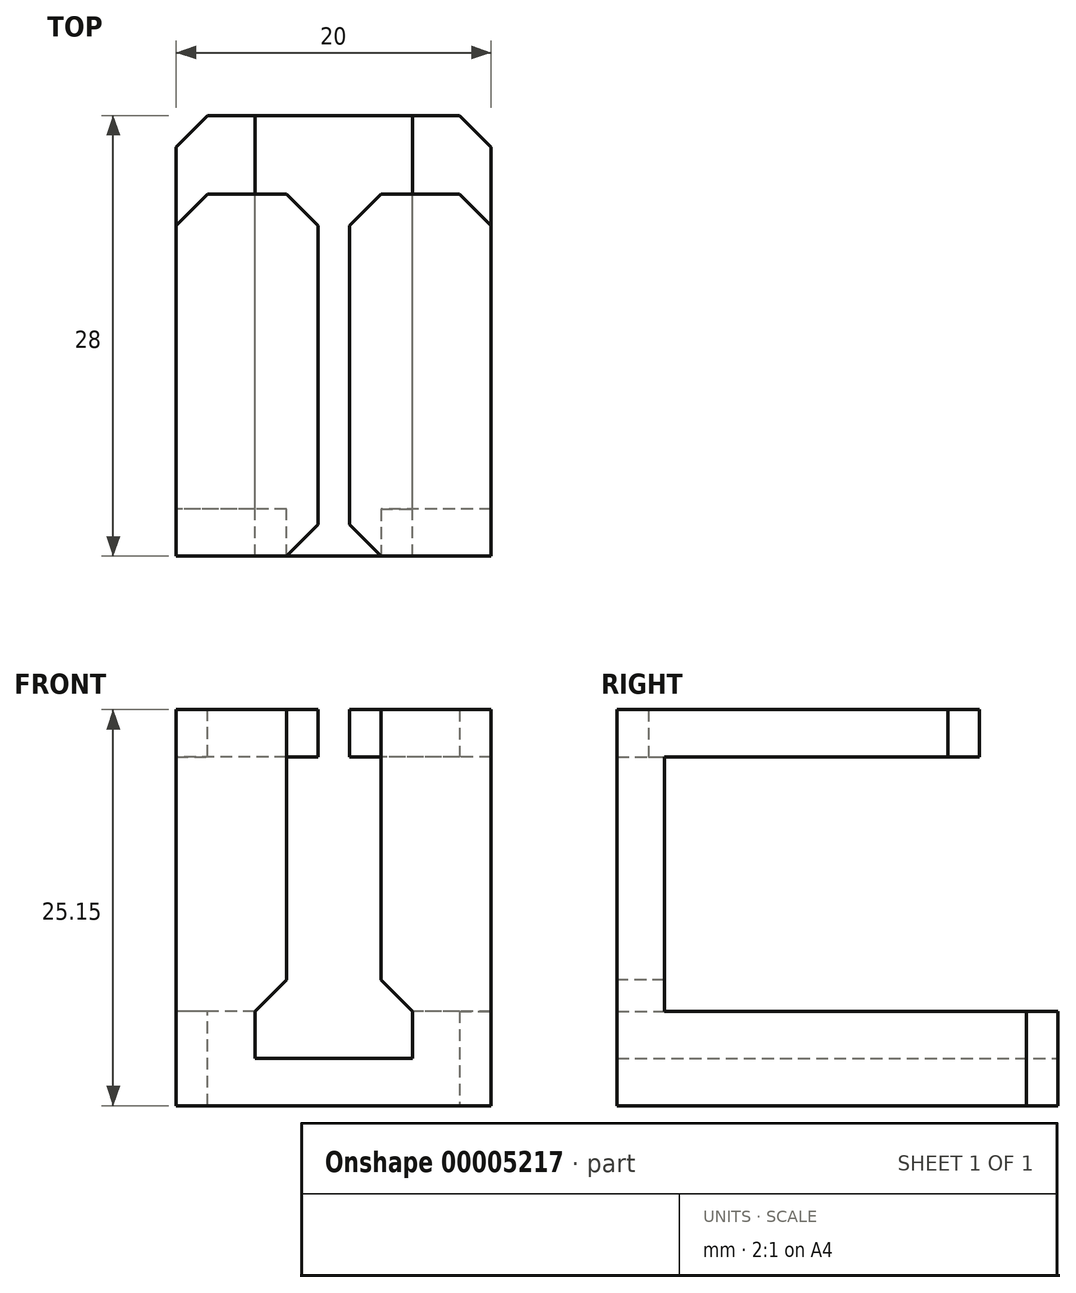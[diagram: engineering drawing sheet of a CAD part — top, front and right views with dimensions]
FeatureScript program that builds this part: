
annotation { "Feature Type Name" : "Feature", "Feature Type Description" : "" }
export const myFeature = defineFeature(function(context is Context, id is Id, definition is map)
    precondition{}
    {
        {
            var Q0;
            Q0=qCreatedBy(makeId("Right.planeOp"),FACE);
            var sketch = newSketch(context, id + "F0", { "sketchPlane" : qUnion([Q0])});
            skLineSegment(sketch, "E0", {"start": v(0, 0) * mm, "end": v(25, 0) * mm});
            skLineSegment(sketch, "E1", {"start": v(25, 0) * mm, "end": v(25, -6) * mm});
            skLineSegment(sketch, "E2", {"start": v(25, -6) * mm, "end": v(-3, -6) * mm});
            skLineSegment(sketch, "E3", {"start": v(-3, -6) * mm, "end": v(-3, 19.15) * mm});
            skLineSegment(sketch, "E4", {"start": v(-3, 19.15) * mm, "end": v(20, 19.15) * mm});
            skLineSegment(sketch, "E5", {"start": v(20, 19.15) * mm, "end": v(20, 16.15) * mm});
            skLineSegment(sketch, "E6", {"start": v(20, 16.15) * mm, "end": v(0, 16.15) * mm});
            skLineSegment(sketch, "E7", {"start": v(0, 16.15) * mm, "end": v(0, 0) * mm});
            skLineSegment(sketch, "E8", {"start": v(0, 16.15) * mm, "end": v(-3, 16.15) * mm, "construction": true});
            skSolve(sketch);
        }
        {
            var Q0;
            Q0 = qSketchRegion(id + "F0", true);
            extrude(context, id + "F1", {"entities" : qUnion([Q0]), "depth" : 20 * mm, "symmetric" : true});
        }
        {
            var Q0;
            Q0=makeQuery(id+"F1.opExtrude","SWEPT_FACE",FACE,{"disambiguationData":[OSD([sQuery(id+"F0.wireOp",EDGE,"E1")])]});
            var sketch = newSketch(context, id + "F2", { "sketchPlane" : qUnion([Q0])});
            skLineSegment(sketch, "E9", {"start": v(0, 0) * mm, "end": v(0, 28.98) * mm, "construction": true});
            skPoint(sketch, "E9.endSnap0", {"position": v(0, 0) * mm});
            skLineSegment(sketch, "E10.bottom", {"start": v(-3, -3) * mm, "end": v(3, -3) * mm});
            skLineSegment(sketch, "E10.top", {"start": v(-3, 19.15) * mm, "end": v(3, 19.15) * mm});
            skLineSegment(sketch, "E10.left", {"start": v(-3, -3) * mm, "end": v(-3, 19.15) * mm});
            skLineSegment(sketch, "E10.right", {"start": v(3, -3) * mm, "end": v(3, 19.15) * mm});
            skLineSegment(sketch, "E11.0", {"start": v(-10, 19.15) * mm, "end": v(10, 19.15) * mm, "construction": true});
            skSolve(sketch);
        }
        {
            var Q0;
            Q0 = qSketchRegion(id + "F2", true);
            extrude(context, id + "F3", {"entities" : qUnion([Q0]), "operationType" : NewBodyOperationType.REMOVE, "endBound" : BoundingType.THROUGH_ALL, "oppositeDirection" : true, "depth" : 25 * mm});
        }
        {
            var Q0;
            Q0=makeQuery(id+"F1.opExtrude","SWEPT_FACE",FACE,{"disambiguationData":[OSD([sQuery(id+"F0.wireOp",EDGE,"E1")])]});
            var sketch = newSketch(context, id + "F4", { "sketchPlane" : qUnion([Q0])});
            skLineSegment(sketch, "E12.bottom", {"start": v(-5, 0) * mm, "end": v(5, 0) * mm});
            skLineSegment(sketch, "E12.top", {"start": v(-5, -3) * mm, "end": v(5, -3) * mm});
            skLineSegment(sketch, "E12.left", {"start": v(-5, 0) * mm, "end": v(-5, -3) * mm});
            skLineSegment(sketch, "E12.right", {"start": v(5, 0) * mm, "end": v(5, -3) * mm});
            skSolve(sketch);
        }
        {
            var Q0;
            Q0 = qSketchRegion(id + "F4", true);
            extrude(context, id + "F5", {"entities" : qUnion([Q0]), "operationType" : NewBodyOperationType.REMOVE, "endBound" : BoundingType.THROUGH_ALL, "oppositeDirection" : true, "depth" : 25 * mm});
        }
        {
            var Q0;
            {var subQ1=sQuery(id+"F0.wireOp",EDGE,"E4");Q0=makeQuery(id+"F3.boolean.opBoolean","SPLIT",FACE,{"disambiguationData":[TD([makeQuery(id+"F3.opExtrude","SWEPT_FACE",FACE,{"disambiguationData":[OSD([sQuery(id+"F2.wireOp",EDGE,"E10.left")])]})])],"derivedFrom":makeQuery(id+"F1.opExtrude","SWEPT_FACE",FACE,{"disambiguationData":[OSD([subQ1])]})});}
            var sketch = newSketch(context, id + "F6", { "sketchPlane" : qUnion([Q0])});
            skLineSegment(sketch, "E13.bottom", {"start": v(3, -3) * mm, "end": v(1, -3) * mm});
            skLineSegment(sketch, "E13.top", {"start": v(3, 20) * mm, "end": v(1, 20) * mm});
            skLineSegment(sketch, "E13.left", {"start": v(3, -3) * mm, "end": v(3, 20) * mm});
            skLineSegment(sketch, "E13.right", {"start": v(1, -3) * mm, "end": v(1, 20) * mm});
            skLineSegment(sketch, "E14", {"start": v(0, 0) * mm, "end": v(0, 7.4) * mm, "construction": true});
            skLineSegment(sketch, "E15.MirrorCS", {"start": v(-3, 20) * mm, "end": v(-1, 20) * mm});
            skLineSegment(sketch, "E16.MirrorCS", {"start": v(-3, -3) * mm, "end": v(-1, -3) * mm});
            skLineSegment(sketch, "E17.MirrorCS", {"start": v(-3, -3) * mm, "end": v(-3, 20) * mm});
            skLineSegment(sketch, "E18.MirrorCS", {"start": v(-1, -3) * mm, "end": v(-1, 20) * mm});
            skSolve(sketch);
        }
        {
            var Q0;
            Q0 = qSketchRegion(id + "F6", true);
            var Q1;
            {var subQ1=sQuery(id+"F0.wireOp",EDGE,"E6");Q1=makeQuery(id+"F3.boolean.opBoolean","SPLIT",FACE,{"disambiguationData":[TD([makeQuery(id+"F3.opExtrude","SWEPT_FACE",FACE,{"disambiguationData":[OSD([sQuery(id+"F2.wireOp",EDGE,"E10.left")])]})])],"derivedFrom":makeQuery(id+"F1.opExtrude","SWEPT_FACE",FACE,{"disambiguationData":[OSD([subQ1])]})});}
            extrude(context, id + "F7", {"entities" : qUnion([Q0]), "operationType" : NewBodyOperationType.ADD, "endBound" : BoundingType.UP_TO_SURFACE, "oppositeDirection" : true, "endBoundEntityFace" : qUnion([Q1]), "depth" : 25 * mm});
        }
        {
            var Q0;
            Q0=makeQuery(id+"F5.boolean.opBoolean","INTERSECT",EDGE,{"derivedFrom":[makeQuery(id+"F3.boolean.opBoolean","COPY",FACE,{"derivedFrom":makeQuery(id+"F3.opExtrude","SWEPT_FACE",FACE,{"disambiguationData":[OSD([sQuery(id+"F2.wireOp",EDGE,"E10.right")])]})}),makeQuery(id+"F5.opExtrude","SWEPT_FACE",FACE,{"disambiguationData":[OSD([sQuery(id+"F4.wireOp",EDGE,"E12.bottom")])]})]});
            var Q1;
            Q1=makeQuery(id+"F5.boolean.opBoolean","INTERSECT",EDGE,{"derivedFrom":[makeQuery(id+"F3.boolean.opBoolean","COPY",FACE,{"derivedFrom":makeQuery(id+"F3.opExtrude","SWEPT_FACE",FACE,{"disambiguationData":[OSD([sQuery(id+"F2.wireOp",EDGE,"E10.left")])]})}),makeQuery(id+"F5.opExtrude","SWEPT_FACE",FACE,{"disambiguationData":[OSD([sQuery(id+"F4.wireOp",EDGE,"E12.bottom")])]})]});
            var Q2;
            Q2=makeQuery(id+"F7.opExtrude","SWEPT_EDGE",EDGE,{"disambiguationData":[OSD([sQuery(id+"F6.wireOp",EDGE,"E16.MirrorCS"),sQuery(id+"F6.wireOp",EDGE,"E18.MirrorCS")])]});
            var Q3;
            Q3=makeQuery(id+"F7.opExtrude","SWEPT_EDGE",EDGE,{"disambiguationData":[OSD([sQuery(id+"F6.wireOp",EDGE,"E13.bottom"),sQuery(id+"F6.wireOp",EDGE,"E13.right")])]});
            var Q4;
            Q4=makeQuery(id+"F7.opExtrude","SWEPT_EDGE",EDGE,{"disambiguationData":[OSD([sQuery(id+"F6.wireOp",EDGE,"E13.top"),sQuery(id+"F6.wireOp",EDGE,"E13.right")])]});
            var Q5;
            Q5=makeQuery(id+"F7.opExtrude","SWEPT_EDGE",EDGE,{"disambiguationData":[OSD([sQuery(id+"F6.wireOp",EDGE,"E15.MirrorCS"),sQuery(id+"F6.wireOp",EDGE,"E18.MirrorCS")])]});
            var Q6;
            Q6=makeQuery(id+"F1.opExtrude","CAP_EDGE",EDGE,{"disambiguationData":[OSD([sQuery(id+"F0.wireOp",EDGE,"E5")])],"isStart":true});
            var Q7;
            Q7=makeQuery(id+"F1.opExtrude","CAP_EDGE",EDGE,{"disambiguationData":[OSD([sQuery(id+"F0.wireOp",EDGE,"E5")])],"isStart":false});
            var Q8;
            Q8=makeQuery(id+"F1.opExtrude","CAP_EDGE",EDGE,{"disambiguationData":[OSD([sQuery(id+"F0.wireOp",EDGE,"E1")])],"isStart":false});
            var Q9;
            Q9=makeQuery(id+"F1.opExtrude","CAP_EDGE",EDGE,{"disambiguationData":[OSD([sQuery(id+"F0.wireOp",EDGE,"E1")])],"isStart":true});
            chamfer(context, id + "F8", {"entities" : qUnion([Q0, Q1, Q2, Q3, Q4, Q5, Q6, Q7, Q8, Q9]), "width" : 2 * mm, "tangentPropagation" : true});
        }
    });
